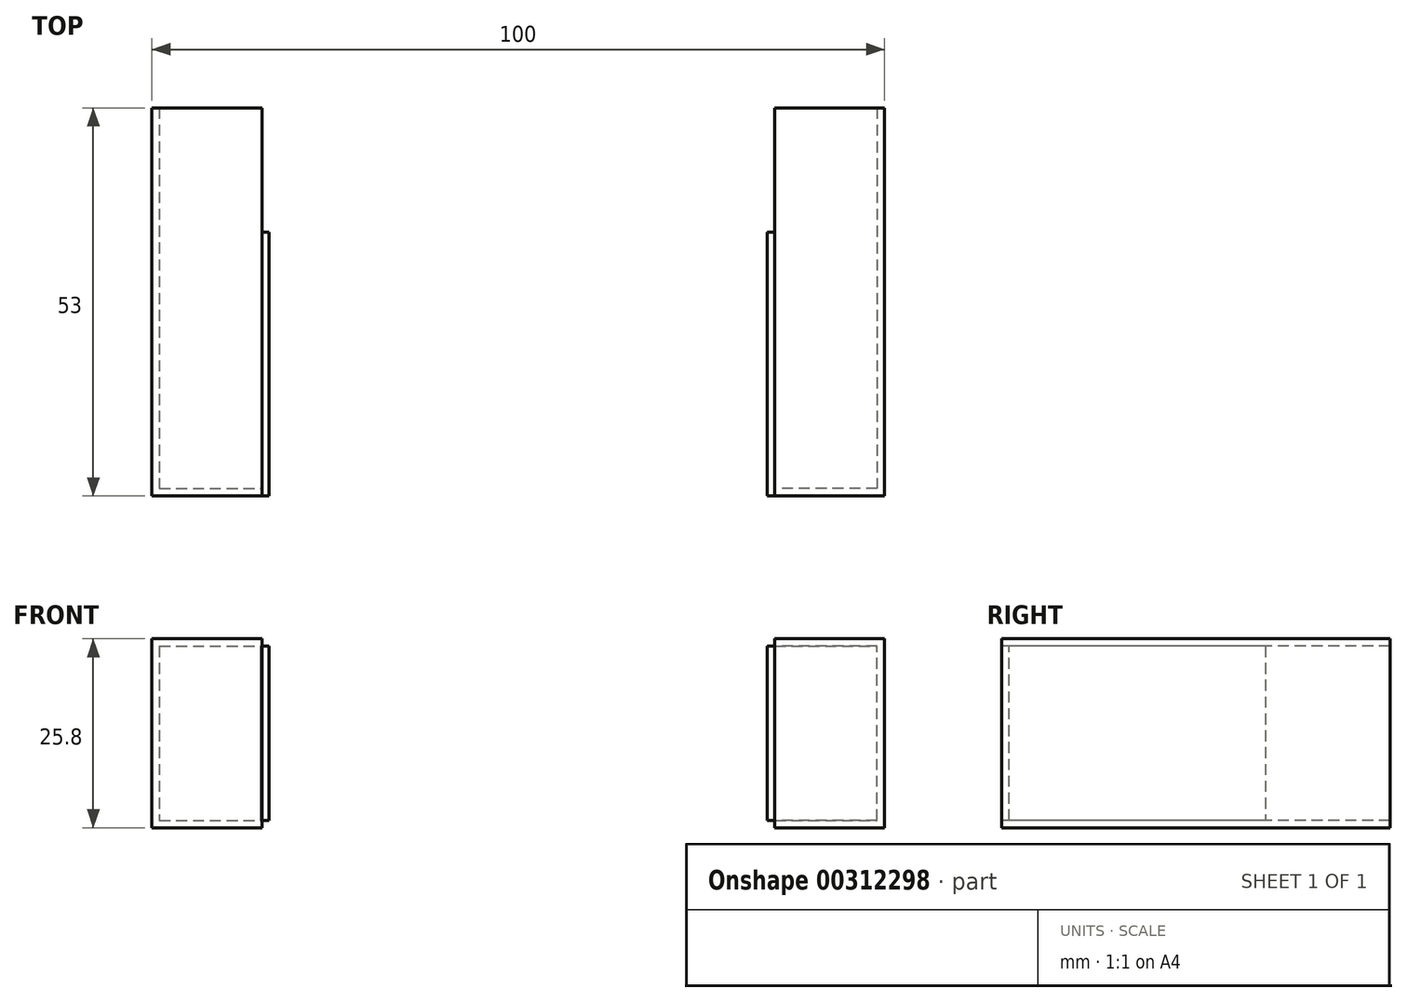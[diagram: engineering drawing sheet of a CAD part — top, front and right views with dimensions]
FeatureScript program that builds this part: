
annotation { "Feature Type Name" : "Feature", "Feature Type Description" : "" }
export const myFeature = defineFeature(function(context is Context, id is Id, definition is map)
    precondition{}
    {
        {
            var Q0;
            Q0=qCreatedBy(makeId("Front.planeOp"),FACE);
            var sketch = newSketch(context, id + "F0", { "sketchPlane" : qUnion([Q0])});
            skLineSegment(sketch, "E0.bottom", {"start": v(-50, 12.9) * mm, "end": v(50, 12.9) * mm});
            skLineSegment(sketch, "E0.top", {"start": v(-50, -12.9) * mm, "end": v(50, -12.9) * mm});
            skLineSegment(sketch, "E0.left", {"start": v(-50, 12.9) * mm, "end": v(-50, -12.9) * mm});
            skLineSegment(sketch, "E0.right", {"start": v(50, 12.9) * mm, "end": v(50, -12.9) * mm});
            skPoint(sketch, "E0.middle", {"position": v(0, 0) * mm});
            skLineSegment(sketch, "E1.bottom", {"start": v(-49, 11.9) * mm, "end": v(49, 11.9) * mm});
            skLineSegment(sketch, "E1.top", {"start": v(-49, -11.9) * mm, "end": v(49, -11.9) * mm});
            skLineSegment(sketch, "E1.left", {"start": v(-49, 11.9) * mm, "end": v(-49, -11.9) * mm});
            skLineSegment(sketch, "E1.right", {"start": v(49, 11.9) * mm, "end": v(49, -11.9) * mm});
            skLineSegment(sketch, "E2.bottom", {"start": v(-35, 12.9) * mm, "end": v(35, 12.9) * mm});
            skLineSegment(sketch, "E2.top", {"start": v(-35, -12.9) * mm, "end": v(35, -12.9) * mm});
            skLineSegment(sketch, "E2.left", {"start": v(-35, 12.9) * mm, "end": v(-35, -12.9) * mm});
            skLineSegment(sketch, "E2.right", {"start": v(35, 12.9) * mm, "end": v(35, -12.9) * mm});
            skLineSegment(sketch, "E3.bottom", {"start": v(-34, 11.9) * mm, "end": v(34, 11.9) * mm});
            skLineSegment(sketch, "E3.top", {"start": v(-34, -11.9) * mm, "end": v(34, -11.9) * mm});
            skLineSegment(sketch, "E3.left", {"start": v(-34, 11.9) * mm, "end": v(-34, -11.9) * mm});
            skLineSegment(sketch, "E3.right", {"start": v(34, 11.9) * mm, "end": v(34, -11.9) * mm});
            skCircle(sketch, "E4", {"center": v(0, 0) * mm, "radius": 3 * mm});
            skLineSegment(sketch, "E5.bottom", {"start": v(34, 0) * mm, "end": v(-34, 0) * mm});
            skLineSegment(sketch, "E5.top", {"start": v(34, 0) * mm, "end": v(-34, 0) * mm});
            skLineSegment(sketch, "E5.left", {"start": v(34, 0) * mm, "end": v(34, 0) * mm});
            skLineSegment(sketch, "E5.right", {"start": v(-34, 0) * mm, "end": v(-34, 0) * mm});
            skLineSegment(sketch, "E6.bottom", {"start": v(34, 3) * mm, "end": v(-34, 3) * mm});
            skLineSegment(sketch, "E6.top", {"start": v(34, -3) * mm, "end": v(-34, -3) * mm});
            skLineSegment(sketch, "E6.left", {"start": v(34, 3) * mm, "end": v(34, -3) * mm});
            skLineSegment(sketch, "E6.right", {"start": v(-34, 3) * mm, "end": v(-34, -3) * mm});
            skSolve(sketch);
        }
        {
            var Q0;
            {var subQ0=sQuery(id+"F0.wireOp",EDGE,"E2.bottom");Q0=makeQuery(id+"F0.imprint","IMPRINT",FACE,{"disambiguationData":[TD([[makeQuery(id+"F0.imprint","IMPRINT",EDGE,{"derivedFrom":subQ0}),-1.0]])]});}
            var Q1;
            {var subQ4=sQuery(id+"F0.wireOp",EDGE,"E0.left");Q1=makeQuery(id+"F0.imprint","IMPRINT",FACE,{"disambiguationData":[TD([[makeQuery(id+"F0.imprint","IMPRINT",EDGE,{"derivedFrom":subQ4}),1.0]])]});}
            var Q2;
            {var subQ1=sQuery(id+"F0.wireOp",EDGE,"E2.top");Q2=makeQuery(id+"F0.imprint","IMPRINT",FACE,{"disambiguationData":[TD([[makeQuery(id+"F0.imprint","IMPRINT",EDGE,{"derivedFrom":subQ1}),1.0]])]});}
            var Q3;
            {var subQ4=sQuery(id+"F0.wireOp",EDGE,"E0.right");Q3=makeQuery(id+"F0.imprint","IMPRINT",FACE,{"disambiguationData":[TD([[makeQuery(id+"F0.imprint","IMPRINT",EDGE,{"derivedFrom":subQ4}),-1.0]])]});}
            extrude(context, id + "F1", {"entities" : qUnion([Q0, Q1, Q2, Q3]), "oppositeDirection" : true, "depth" : 53 * mm});
        }
        {
            var Q0;
            {var subQ0=sQuery(id+"F0.wireOp",EDGE,"E3.left");Q0=makeQuery(id+"F0.imprint","IMPRINT",FACE,{"disambiguationData":[TD([[makeQuery(id+"F0.imprint","IMPRINT",EDGE,{"derivedFrom":subQ0}),-1.0]])]});}
            var Q1;
            {var subQ0=sQuery(id+"F0.wireOp",EDGE,"E3.right");Q1=makeQuery(id+"F0.imprint","IMPRINT",FACE,{"disambiguationData":[TD([[makeQuery(id+"F0.imprint","IMPRINT",EDGE,{"derivedFrom":subQ0}),1.0]])]});}
            extrude(context, id + "F2", {"entities" : qUnion([Q0, Q1]), "operationType" : NewBodyOperationType.ADD, "oppositeDirection" : true, "depth" : 36 * mm});
        }
        {
            var Q0;
            Q0=qCreatedBy(makeId("Top.planeOp"),FACE);
            var sketch = newSketch(context, id + "F3", { "sketchPlane" : qUnion([Q0])});
            skLineSegment(sketch, "E7.bottom", {"start": v(-50, 0) * mm, "end": v(-35, 0) * mm});
            skLineSegment(sketch, "E7.top", {"start": v(-50, 1) * mm, "end": v(-35, 1) * mm});
            skLineSegment(sketch, "E7.left", {"start": v(-50, 0) * mm, "end": v(-50, 1) * mm});
            skLineSegment(sketch, "E7.right", {"start": v(-35, 0) * mm, "end": v(-35, 1) * mm});
            skLineSegment(sketch, "E8.MirrorCS", {"start": v(50, 0) * mm, "end": v(50, 1) * mm});
            skLineSegment(sketch, "E9.MirrorCS", {"start": v(35, 0) * mm, "end": v(35, 1) * mm});
            skLineSegment(sketch, "E10.MirrorCS", {"start": v(50, 0) * mm, "end": v(35, 0) * mm});
            skLineSegment(sketch, "E11.MirrorCS", {"start": v(50, 1) * mm, "end": v(35, 1) * mm});
            skLineSegment(sketch, "E12", {"start": v(-35, 1) * mm, "end": v(35, 1) * mm});
            skSolve(sketch);
        }
        {
            var Q0;
            Q0=makeQuery(id+"F3.imprint","IMPRINT",FACE,{"disambiguationData":[TD([[makeQuery(id+"F3.imprint","IMPRINT",EDGE,{"derivedFrom":sQuery(id+"F3.wireOp",EDGE,"E10.MirrorCS")}),-1.0]])]});
            var Q1;
            Q1=makeQuery(id+"F3.imprint","IMPRINT",FACE,{"disambiguationData":[TD([[makeQuery(id+"F3.imprint","IMPRINT",EDGE,{"derivedFrom":sQuery(id+"F3.wireOp",EDGE,"E7.bottom")}),1.0]])]});
            extrude(context, id + "F4", {"entities" : qUnion([Q0, Q1]), "operationType" : NewBodyOperationType.ADD, "depth" : 23.8 * mm, "symmetric" : true});
        }
    });
